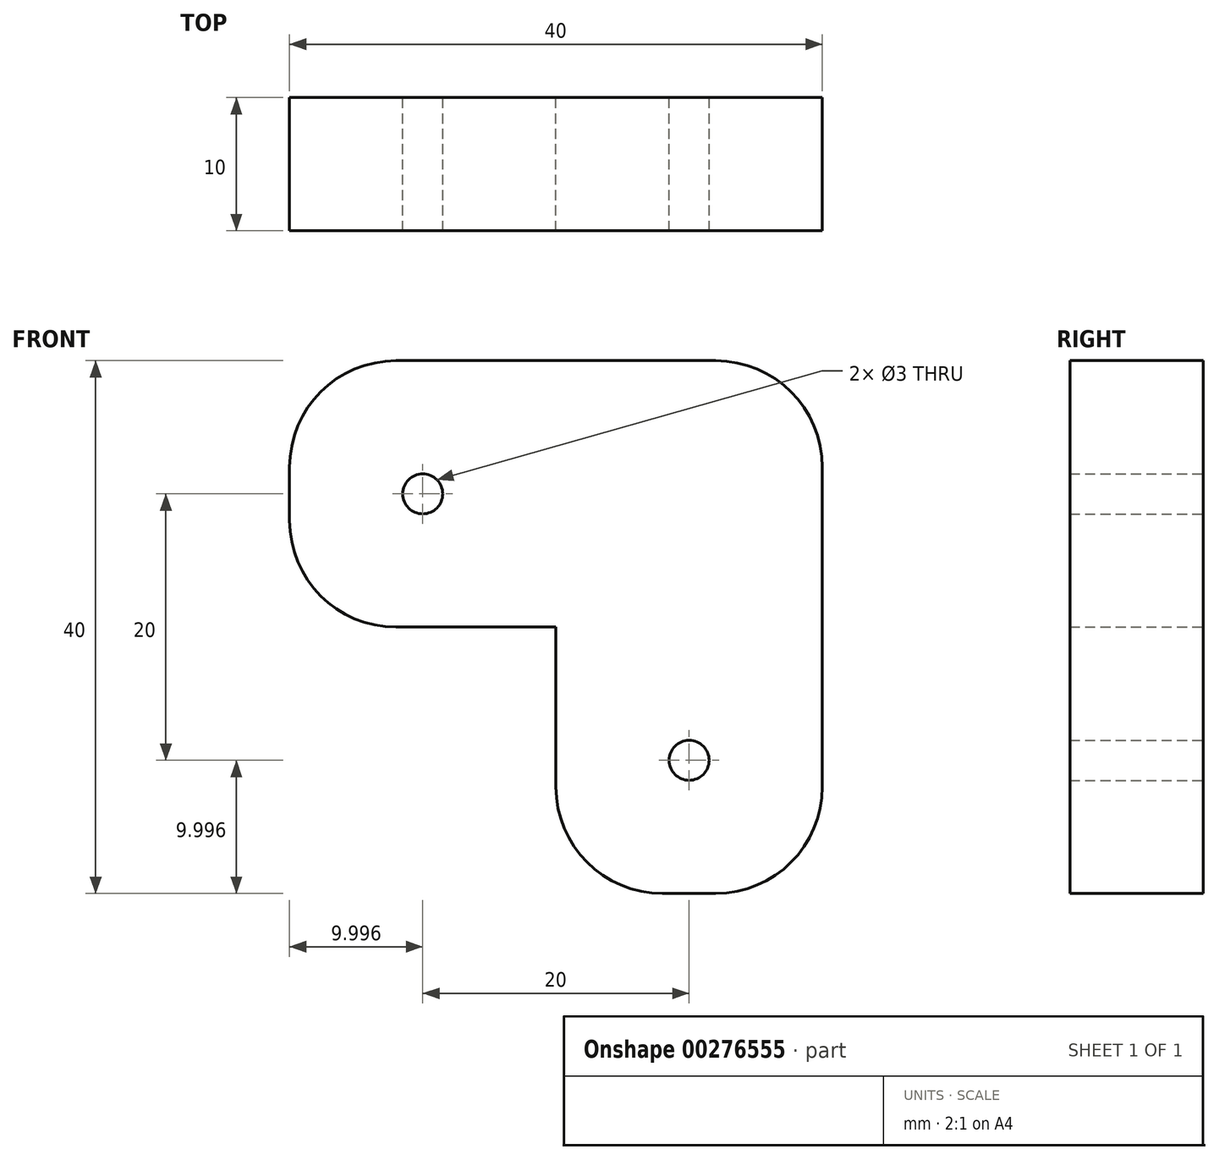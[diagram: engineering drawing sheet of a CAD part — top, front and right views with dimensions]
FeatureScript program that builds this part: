
annotation { "Feature Type Name" : "Feature", "Feature Type Description" : "" }
export const myFeature = defineFeature(function(context is Context, id is Id, definition is map)
    precondition{}
    {
        {
            var Q0;
            Q0=qCreatedBy(makeId("Front.planeOp"),FACE);
            var sketch = newSketch(context, id + "F0", { "sketchPlane" : qUnion([Q0])});
            skLineSegment(sketch, "E0.bottom", {"start": v(-7.15, -22.91) * mm, "end": v(-27.15, -22.91) * mm});
            skLineSegment(sketch, "E0.left", {"start": v(-7.15, -22.91) * mm, "end": v(-7.15, -2.91) * mm});
            skLineSegment(sketch, "E0.right", {"start": v(-27.15, -22.91) * mm, "end": v(-27.15, -2.91) * mm});
            skPoint(sketch, "E0.middle", {"position": v(-17.15, -12.91) * mm});
            skLineSegment(sketch, "E1.bottom", {"start": v(-27.15, -2.91) * mm, "end": v(-47.15, -2.91) * mm});
            skLineSegment(sketch, "E1.top", {"start": v(-27.15, 17.09) * mm, "end": v(-47.15, 17.09) * mm});
            skLineSegment(sketch, "E1.right", {"start": v(-47.15, -2.91) * mm, "end": v(-47.15, 17.09) * mm});
            skLineSegment(sketch, "E2", {"start": v(-27.15, 17.09) * mm, "end": v(-7.15, 17.09) * mm});
            skLineSegment(sketch, "E3", {"start": v(-7.15, 17.09) * mm, "end": v(-7.15, -2.91) * mm});
            skCircle(sketch, "E4", {"center": v(-17.15, -12.91) * mm, "radius": 1.5 * mm});
            skLineSegment(sketch, "E5", {"start": v(-27.15, -2.91) * mm, "end": v(-7.15, 17.09) * mm, "construction": true});
            skCircle(sketch, "E6.MirrorC", {"center": v(-37.15, 7.09) * mm, "radius": 1.5 * mm});
            skSolve(sketch);
        }
        {
            var Q0;
            Q0 = qSketchRegion(id + "F0", true);
            extrude(context, id + "F1", {"entities" : qUnion([Q0]), "depth" : 10 * mm, "offsetDistance" : 25 * mm});
        }
        {
            var Q0;
            Q0=makeQuery(id+"F1.opExtrude","SWEPT_EDGE",EDGE,{"disambiguationData":[OSD([sQuery(id+"F0.wireOp",EDGE,"E2"),sQuery(id+"F0.wireOp",EDGE,"E3")])]});
            var Q1;
            Q1=makeQuery(id+"F1.opExtrude","SWEPT_EDGE",EDGE,{"disambiguationData":[OSD([sQuery(id+"F0.wireOp",EDGE,"E1.top"),sQuery(id+"F0.wireOp",EDGE,"E1.right")])]});
            var Q2;
            Q2=makeQuery(id+"F1.opExtrude","SWEPT_EDGE",EDGE,{"disambiguationData":[OSD([sQuery(id+"F0.wireOp",EDGE,"E1.bottom"),sQuery(id+"F0.wireOp",EDGE,"E1.right")])]});
            var Q3;
            Q3=makeQuery(id+"F1.opExtrude","SWEPT_EDGE",EDGE,{"disambiguationData":[OSD([sQuery(id+"F0.wireOp",EDGE,"E0.bottom"),sQuery(id+"F0.wireOp",EDGE,"E0.right")])]});
            var Q4;
            Q4=makeQuery(id+"F1.opExtrude","SWEPT_EDGE",EDGE,{"disambiguationData":[OSD([sQuery(id+"F0.wireOp",EDGE,"E0.bottom"),sQuery(id+"F0.wireOp",EDGE,"E0.left")])]});
            fillet(context, id + "F2", {"entities" : qUnion([Q0, Q1, Q2, Q3, Q4]), "tangentPropagation" : true, "radius" : 8 * mm, "defaultsChanged" : true, "vertexSettings" : [], "allowEdgeOverflow" : false});
        }
    });
